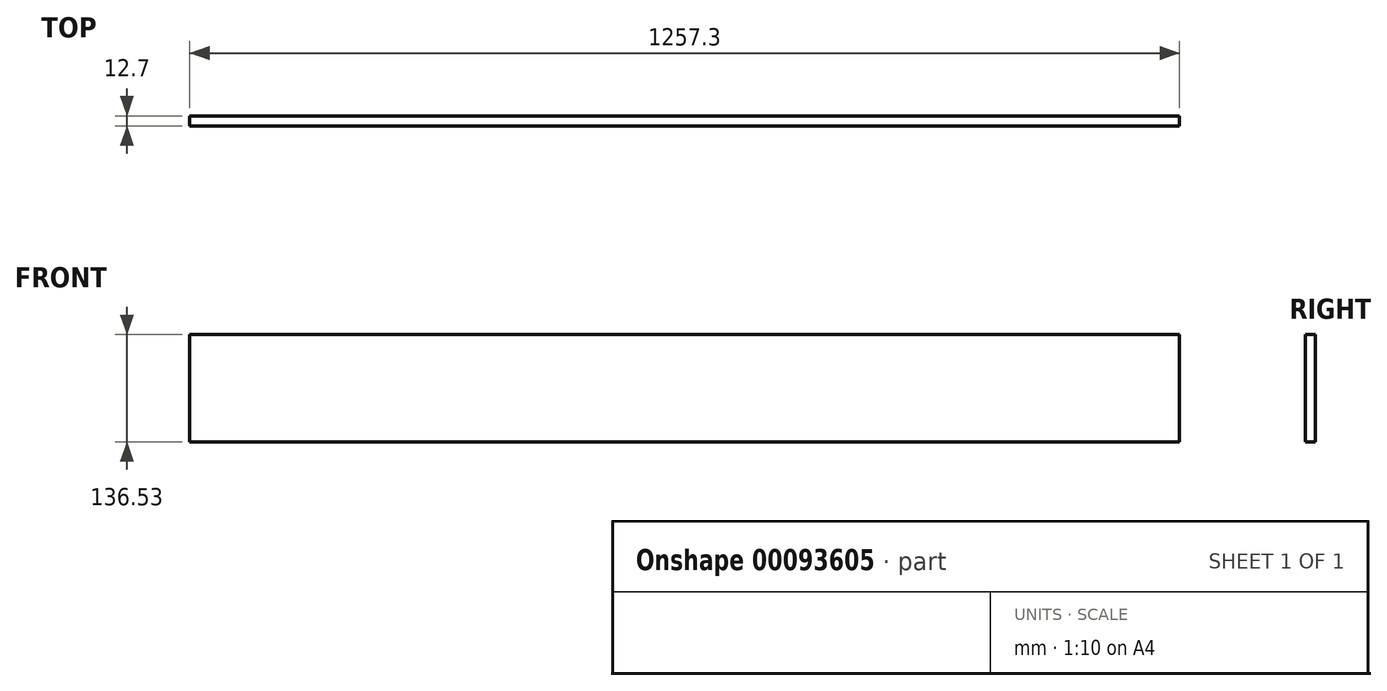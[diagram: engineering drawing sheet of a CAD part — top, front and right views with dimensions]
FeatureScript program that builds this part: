
annotation { "Feature Type Name" : "Feature", "Feature Type Description" : "" }
export const myFeature = defineFeature(function(context is Context, id is Id, definition is map)
    precondition{}
    {
        {
            var Q0;
            Q0=qCreatedBy(makeId("Front.planeOp"),FACE);
            var sketch = newSketch(context, id + "F0", { "sketchPlane" : qUnion([Q0])});
            skLineSegment(sketch, "E0.bottom", {"start": v(0, 0) * mm, "end": v(1257.3, 0) * mm});
            skLineSegment(sketch, "E0.top", {"start": v(0, 136.53) * mm, "end": v(1257.3, 136.53) * mm});
            skLineSegment(sketch, "E0.left", {"start": v(0, 0) * mm, "end": v(0, 136.53) * mm});
            skLineSegment(sketch, "E0.right", {"start": v(1257.3, 0) * mm, "end": v(1257.3, 136.53) * mm});
            skSolve(sketch);
        }
        {
            var Q0;
            Q0 = qSketchRegion(id + "F0", true);
            extrude(context, id + "F1", {"entities" : qUnion([Q0]), "depth" : 12.7 * mm});
        }
    });
